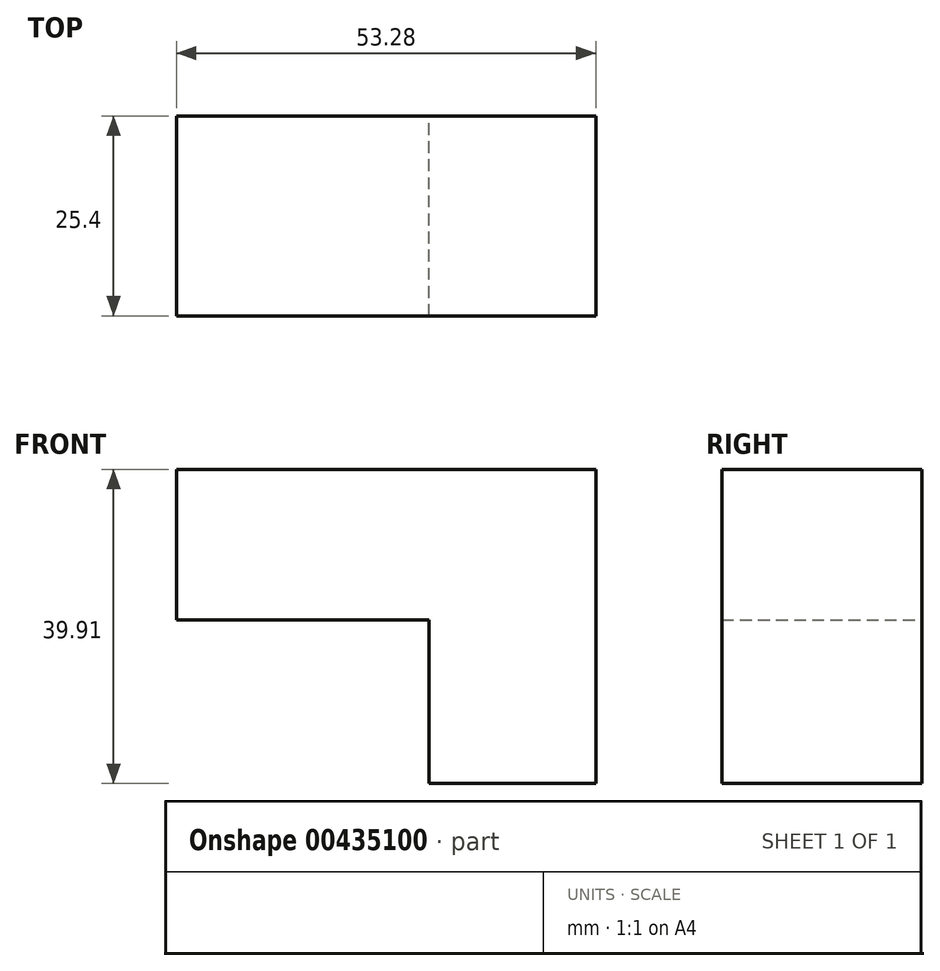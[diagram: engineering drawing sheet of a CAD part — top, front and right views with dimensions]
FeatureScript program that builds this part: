
annotation { "Feature Type Name" : "Feature", "Feature Type Description" : "" }
export const myFeature = defineFeature(function(context is Context, id is Id, definition is map)
    precondition{}
    {
        {
            var Q0;
            Q0=qCreatedBy(makeId("Front.planeOp"),FACE);
            var sketch = newSketch(context, id + "F0", { "sketchPlane" : qUnion([Q0])});
            skLineSegment(sketch, "E0", {"start": v(0, 0) * mm, "end": v(0, 39.9) * mm});
            skLineSegment(sketch, "E1", {"start": v(0, 39.9) * mm, "end": v(-53.28, 39.9) * mm});
            skLineSegment(sketch, "E2", {"start": v(-53.28, 39.9) * mm, "end": v(-53.28, 20.81) * mm});
            skLineSegment(sketch, "E3", {"start": v(-53.28, 20.81) * mm, "end": v(-21.2, 20.81) * mm});
            skLineSegment(sketch, "E4", {"start": v(-21.2, 20.81) * mm, "end": v(-21.2, 0) * mm});
            skLineSegment(sketch, "E5", {"start": v(-21.2, 0) * mm, "end": v(0, 0) * mm});
            skSolve(sketch);
        }
        {
            var Q0;
            Q0 = qSketchRegion(id + "F0", true);
            extrude(context, id + "F1", {"entities" : qUnion([Q0]), "depth" : 25.4 * mm});
        }
    });
